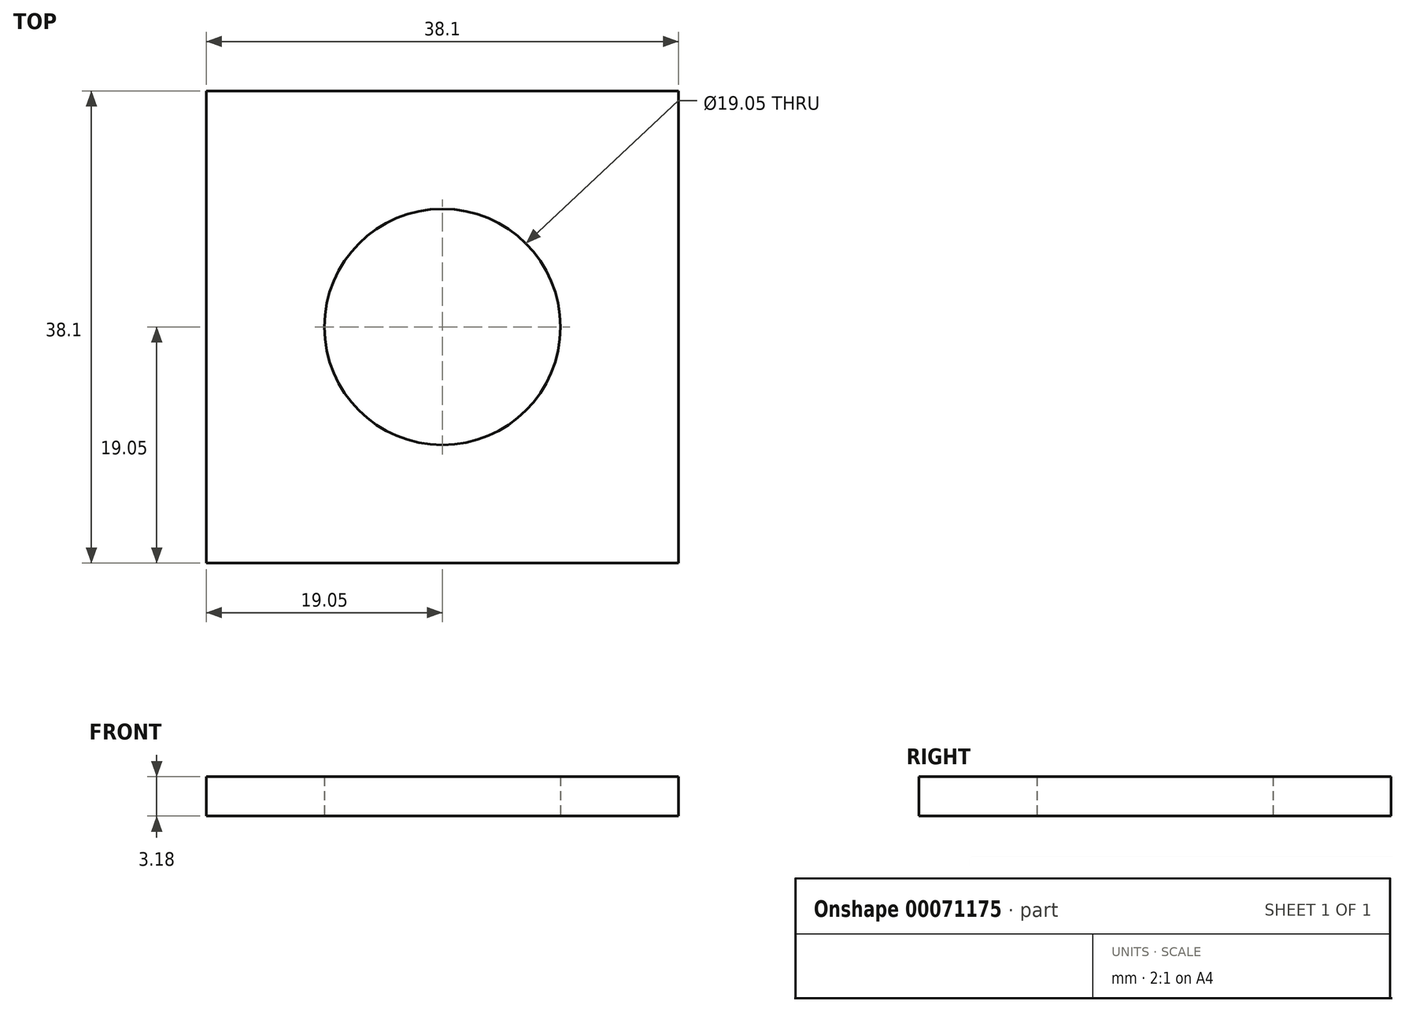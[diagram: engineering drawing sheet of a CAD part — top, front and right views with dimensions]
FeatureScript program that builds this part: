
annotation { "Feature Type Name" : "Feature", "Feature Type Description" : "" }
export const myFeature = defineFeature(function(context is Context, id is Id, definition is map)
    precondition{}
    {
        {
            var Q0;
            Q0=qCreatedBy(makeId("Top.planeOp"),FACE);
            var sketch = newSketch(context, id + "F0", { "sketchPlane" : qUnion([Q0])});
            skLineSegment(sketch, "E0.rect.bottom", {"start": v(19.05, 19.05) * mm, "end": v(-19.05, 19.05) * mm});
            skLineSegment(sketch, "E0.rect.top", {"start": v(19.05, -19.05) * mm, "end": v(-19.05, -19.05) * mm});
            skLineSegment(sketch, "E0.rect.left", {"start": v(19.05, 19.05) * mm, "end": v(19.05, -19.05) * mm});
            skLineSegment(sketch, "E0.rect.right", {"start": v(-19.05, 19.05) * mm, "end": v(-19.05, -19.05) * mm});
            skPoint(sketch, "E0.rect.middle", {"position": v(0, 0) * mm});
            skCircle(sketch, "E1", {"center": v(0, 0) * mm, "radius": 9.53 * mm});
            skSolve(sketch);
        }
        {
            var Q0;
            Q0=makeQuery(id+"F0.imprint","IMPRINT",FACE,{"disambiguationData":[TD([[makeQuery(id+"F0.imprint","IMPRINT",EDGE,{"derivedFrom":sQuery(id+"F0.wireOp",EDGE,"E0.rect.bottom")}),1.0]])]});
            extrude(context, id + "F1", {"entities" : qUnion([Q0]), "depth" : 3.17 * mm});
        }
    });
